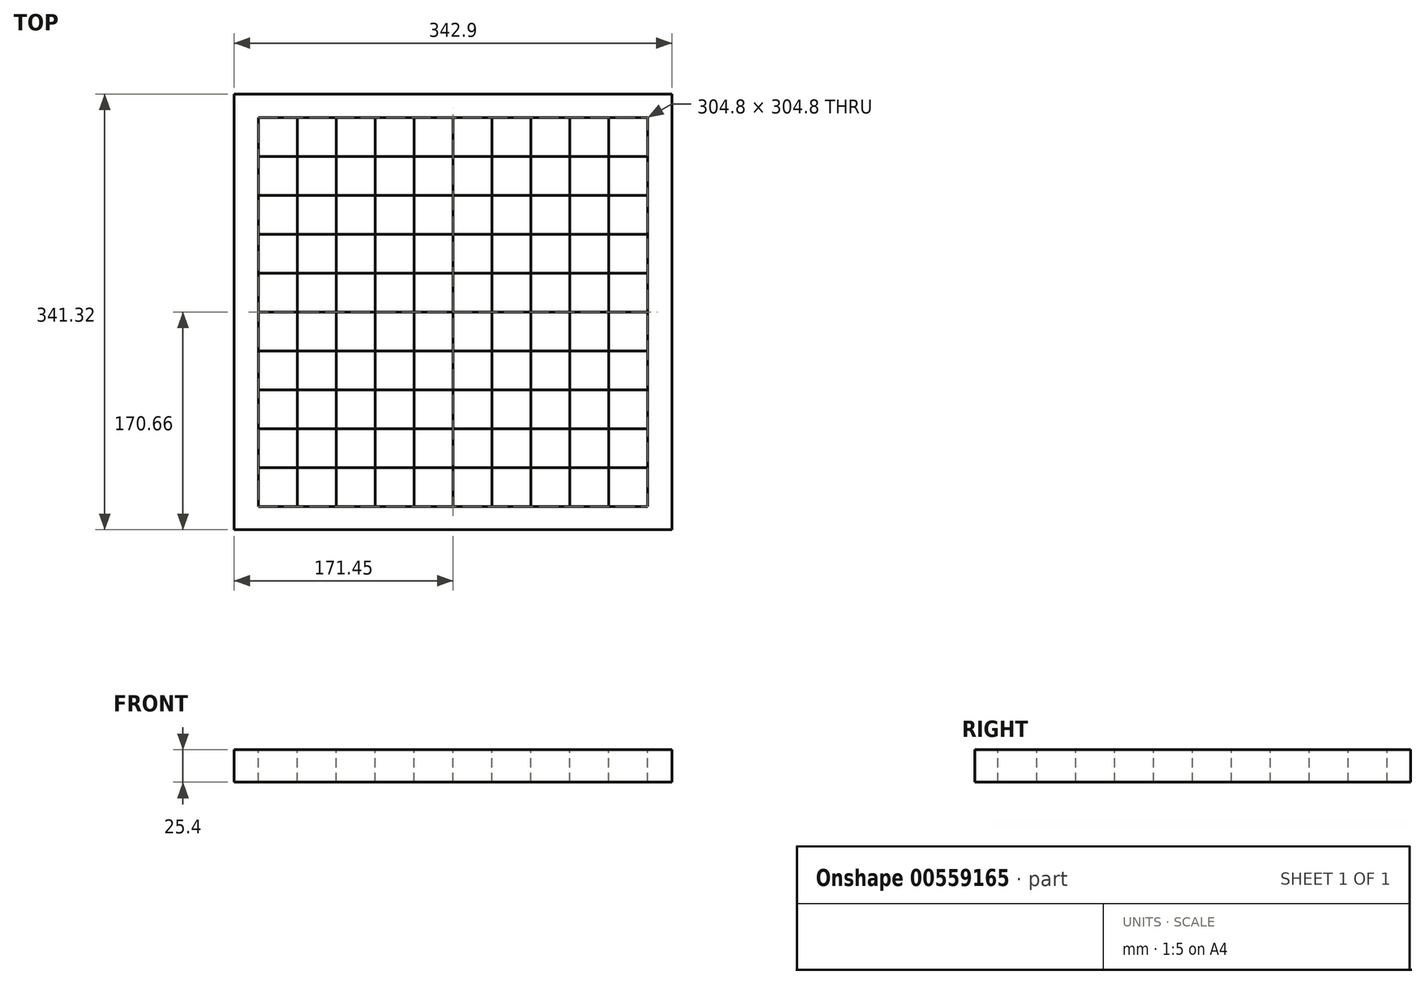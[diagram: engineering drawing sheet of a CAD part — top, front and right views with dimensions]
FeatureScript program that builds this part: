
annotation { "Feature Type Name" : "Feature", "Feature Type Description" : "" }
export const myFeature = defineFeature(function(context is Context, id is Id, definition is map)
    precondition{}
    {
        {
            var Q0;
            Q0=qCreatedBy(makeId("Top.planeOp"),FACE);
            var sketch = newSketch(context, id + "F0", { "sketchPlane" : qUnion([Q0])});
            skLineSegment(sketch, "E0.bottom", {"start": v(171.45, -170.66) * mm, "end": v(-171.45, -170.66) * mm});
            skLineSegment(sketch, "E0.top", {"start": v(171.45, 170.66) * mm, "end": v(-171.45, 170.66) * mm});
            skLineSegment(sketch, "E0.left", {"start": v(171.45, -170.66) * mm, "end": v(171.45, 170.66) * mm});
            skLineSegment(sketch, "E0.right", {"start": v(-171.45, -170.66) * mm, "end": v(-171.45, 170.66) * mm});
            skPoint(sketch, "E0.middle", {"position": v(0, 0) * mm});
            skLineSegment(sketch, "E1.bottom", {"start": v(152.4, -152.4) * mm, "end": v(-152.4, -152.4) * mm});
            skLineSegment(sketch, "E1.top", {"start": v(152.4, 152.4) * mm, "end": v(-152.4, 152.4) * mm});
            skLineSegment(sketch, "E1.left", {"start": v(152.4, -152.4) * mm, "end": v(152.4, 152.4) * mm});
            skLineSegment(sketch, "E1.right", {"start": v(-152.4, -152.4) * mm, "end": v(-152.4, 152.4) * mm});
            skSolve(sketch);
        }
        {
            var Q0;
            Q0=makeQuery(id+"F0.imprint","IMPRINT",FACE,{"disambiguationData":[TD([[makeQuery(id+"F0.imprint","IMPRINT",EDGE,{"derivedFrom":sQuery(id+"F0.wireOp",EDGE,"E1.bottom")}),-1.0]])]});
            var sketch = newSketch(context, id + "F1", { "sketchPlane" : qUnion([Q0])});
            skLineSegment(sketch, "E2.0", {"start": v(152.4, 152.4) * mm, "end": v(-152.4, 152.4) * mm});
            skLineSegment(sketch, "E3.0", {"start": v(-152.4, -152.4) * mm, "end": v(-152.4, 152.4) * mm});
            skLineSegment(sketch, "E4.0", {"start": v(152.4, -152.4) * mm, "end": v(-152.4, -152.4) * mm});
            skLineSegment(sketch, "E5.0", {"start": v(152.4, -152.4) * mm, "end": v(152.4, 152.4) * mm});
            skLineSegment(sketch, "E6", {"start": v(-121.92, 152.4) * mm, "end": v(-121.92, -152.4) * mm});
            skLineSegment(sketch, "E7", {"start": v(-91.44, 152.4) * mm, "end": v(-91.44, -152.4) * mm});
            skLineSegment(sketch, "E8", {"start": v(-60.96, 152.4) * mm, "end": v(-60.96, -152.4) * mm});
            skLineSegment(sketch, "E9", {"start": v(60.96, 152.4) * mm, "end": v(60.96, -152.4) * mm});
            skLineSegment(sketch, "E10", {"start": v(-30.48, 152.4) * mm, "end": v(-30.48, -152.4) * mm});
            skLineSegment(sketch, "E11", {"start": v(30.48, 152.4) * mm, "end": v(30.48, -152.4) * mm});
            skLineSegment(sketch, "E12", {"start": v(91.44, 152.4) * mm, "end": v(91.44, -152.4) * mm});
            skLineSegment(sketch, "E13", {"start": v(121.92, 152.4) * mm, "end": v(121.92, -152.4) * mm});
            skLineSegment(sketch, "E14", {"start": v(0, 152.4) * mm, "end": v(0, -152.4) * mm});
            skLineSegment(sketch, "E15", {"start": v(-152.4, 121.92) * mm, "end": v(152.4, 121.92) * mm});
            skLineSegment(sketch, "E16", {"start": v(-152.4, 91.44) * mm, "end": v(152.4, 91.44) * mm});
            skLineSegment(sketch, "E17.MirrorCS", {"start": v(-152.4, -121.92) * mm, "end": v(152.4, -121.92) * mm});
            skLineSegment(sketch, "E18.MirrorCS", {"start": v(-152.4, -91.44) * mm, "end": v(152.4, -91.44) * mm});
            skLineSegment(sketch, "E19", {"start": v(-152.4, 60.96) * mm, "end": v(152.4, 60.96) * mm});
            skLineSegment(sketch, "E20", {"start": v(-152.4, 30.48) * mm, "end": v(152.4, 30.48) * mm});
            skLineSegment(sketch, "E21.MirrorCS", {"start": v(-152.4, -60.96) * mm, "end": v(152.4, -60.96) * mm});
            skLineSegment(sketch, "E22.MirrorCS", {"start": v(-152.4, -30.48) * mm, "end": v(152.4, -30.48) * mm});
            skLineSegment(sketch, "E23", {"start": v(-152.4, 0) * mm, "end": v(152.4, 0) * mm});
            skSolve(sketch);
        }
        {
            var Q0;
            Q0 = qSketchRegion(id + "F0", true);
            extrude(context, id + "F2", {"entities" : qUnion([Q0]), "oppositeDirection" : true, "depth" : 25.4 * mm, "offsetDistance" : 25.4 * mm});
        }
        {
            var Q0;
            {var subQ0=sQuery(id+"F1.wireOp",EDGE,"E3.0");var subQ1=sQuery(id+"F1.wireOp",EDGE,"E2.0");var subQ2=makeQuery(id+"F1.imprint","INTERSECT",VERTEX,{"derivedFrom":[subQ1,subQ0]});Q0=makeQuery(id+"F1.imprint","IMPRINT",FACE,{"disambiguationData":[TD([[makeQuery(id+"F1.imprint","IMPRINT",EDGE,{"disambiguationData":[TD([[subQ2,1.0]])],"derivedFrom":subQ1}),1.0]])]});}
            var Q1;
            {var subQ0=sQuery(id+"F1.wireOp",EDGE,"E15");var subQ1=sQuery(id+"F1.wireOp",EDGE,"E6");var subQ2=makeQuery(id+"F1.imprint","INTERSECT",VERTEX,{"derivedFrom":[subQ1,subQ0]});Q1=makeQuery(id+"F1.imprint","IMPRINT",FACE,{"disambiguationData":[TD([[makeQuery(id+"F1.imprint","IMPRINT",EDGE,{"disambiguationData":[TD([[subQ2,-1.0]])],"derivedFrom":subQ1}),1.0]])]});}
            var Q2;
            {var subQ0=sQuery(id+"F1.wireOp",EDGE,"E7");var subQ1=sQuery(id+"F1.wireOp",EDGE,"E2.0");var subQ2=makeQuery(id+"F1.imprint","INTERSECT",VERTEX,{"derivedFrom":[subQ1,subQ0]});Q2=makeQuery(id+"F1.imprint","IMPRINT",FACE,{"disambiguationData":[TD([[makeQuery(id+"F1.imprint","IMPRINT",EDGE,{"disambiguationData":[TD([[subQ2,1.0]])],"derivedFrom":subQ1}),1.0]])]});}
            var Q3;
            {var subQ0=sQuery(id+"F1.wireOp",EDGE,"E15");var subQ1=sQuery(id+"F1.wireOp",EDGE,"E8");var subQ2=makeQuery(id+"F1.imprint","INTERSECT",VERTEX,{"derivedFrom":[subQ1,subQ0]});Q3=makeQuery(id+"F1.imprint","IMPRINT",FACE,{"disambiguationData":[TD([[makeQuery(id+"F1.imprint","IMPRINT",EDGE,{"disambiguationData":[TD([[subQ2,-1.0]])],"derivedFrom":subQ1}),1.0]])]});}
            var Q4;
            {var subQ0=sQuery(id+"F1.wireOp",EDGE,"E10");var subQ1=sQuery(id+"F1.wireOp",EDGE,"E2.0");var subQ2=makeQuery(id+"F1.imprint","INTERSECT",VERTEX,{"derivedFrom":[subQ1,subQ0]});Q4=makeQuery(id+"F1.imprint","IMPRINT",FACE,{"disambiguationData":[TD([[makeQuery(id+"F1.imprint","IMPRINT",EDGE,{"disambiguationData":[TD([[subQ2,1.0]])],"derivedFrom":subQ1}),1.0]])]});}
            var Q5;
            {var subQ0=sQuery(id+"F1.wireOp",EDGE,"E15");var subQ1=sQuery(id+"F1.wireOp",EDGE,"E11");var subQ2=makeQuery(id+"F1.imprint","INTERSECT",VERTEX,{"derivedFrom":[subQ1,subQ0]});Q5=makeQuery(id+"F1.imprint","IMPRINT",FACE,{"disambiguationData":[TD([[makeQuery(id+"F1.imprint","IMPRINT",EDGE,{"disambiguationData":[TD([[subQ2,-1.0]])],"derivedFrom":subQ1}),-1.0]])]});}
            var Q6;
            {var subQ0=sQuery(id+"F1.wireOp",EDGE,"E9");var subQ1=sQuery(id+"F1.wireOp",EDGE,"E2.0");var subQ2=makeQuery(id+"F1.imprint","INTERSECT",VERTEX,{"derivedFrom":[subQ1,subQ0]});Q6=makeQuery(id+"F1.imprint","IMPRINT",FACE,{"disambiguationData":[TD([[makeQuery(id+"F1.imprint","IMPRINT",EDGE,{"disambiguationData":[TD([[subQ2,-1.0]])],"derivedFrom":subQ1}),1.0]])]});}
            var Q7;
            {var subQ0=sQuery(id+"F1.wireOp",EDGE,"E15");var subQ1=sQuery(id+"F1.wireOp",EDGE,"E9");var subQ2=makeQuery(id+"F1.imprint","INTERSECT",VERTEX,{"derivedFrom":[subQ1,subQ0]});Q7=makeQuery(id+"F1.imprint","IMPRINT",FACE,{"disambiguationData":[TD([[makeQuery(id+"F1.imprint","IMPRINT",EDGE,{"disambiguationData":[TD([[subQ2,-1.0]])],"derivedFrom":subQ1}),1.0]])]});}
            var Q8;
            {var subQ0=sQuery(id+"F1.wireOp",EDGE,"E12");var subQ1=sQuery(id+"F1.wireOp",EDGE,"E2.0");var subQ2=makeQuery(id+"F1.imprint","INTERSECT",VERTEX,{"derivedFrom":[subQ1,subQ0]});Q8=makeQuery(id+"F1.imprint","IMPRINT",FACE,{"disambiguationData":[TD([[makeQuery(id+"F1.imprint","IMPRINT",EDGE,{"disambiguationData":[TD([[subQ2,1.0]])],"derivedFrom":subQ1}),1.0]])]});}
            var Q9;
            {var subQ0=sQuery(id+"F1.wireOp",EDGE,"E15");var subQ1=sQuery(id+"F1.wireOp",EDGE,"E5.0");var subQ2=makeQuery(id+"F1.imprint","INTERSECT",VERTEX,{"derivedFrom":[subQ1,subQ0]});Q9=makeQuery(id+"F1.imprint","IMPRINT",FACE,{"disambiguationData":[TD([[makeQuery(id+"F1.imprint","IMPRINT",EDGE,{"disambiguationData":[TD([[subQ2,1.0]])],"derivedFrom":subQ1}),1.0]])]});}
            var Q10;
            {var subQ0=sQuery(id+"F1.wireOp",EDGE,"E16");var subQ1=sQuery(id+"F1.wireOp",EDGE,"E3.0");var subQ2=makeQuery(id+"F1.imprint","INTERSECT",VERTEX,{"derivedFrom":[subQ1,subQ0]});Q10=makeQuery(id+"F1.imprint","IMPRINT",FACE,{"disambiguationData":[TD([[makeQuery(id+"F1.imprint","IMPRINT",EDGE,{"disambiguationData":[TD([[subQ2,1.0]])],"derivedFrom":subQ1}),-1.0]])]});}
            var Q11;
            {var subQ0=sQuery(id+"F1.wireOp",EDGE,"E16");var subQ1=sQuery(id+"F1.wireOp",EDGE,"E7");var subQ2=makeQuery(id+"F1.imprint","INTERSECT",VERTEX,{"derivedFrom":[subQ1,subQ0]});Q11=makeQuery(id+"F1.imprint","IMPRINT",FACE,{"disambiguationData":[TD([[makeQuery(id+"F1.imprint","IMPRINT",EDGE,{"disambiguationData":[TD([[subQ2,-1.0]])],"derivedFrom":subQ1}),1.0]])]});}
            var Q12;
            {var subQ0=sQuery(id+"F1.wireOp",EDGE,"E16");var subQ1=sQuery(id+"F1.wireOp",EDGE,"E10");var subQ2=makeQuery(id+"F1.imprint","INTERSECT",VERTEX,{"derivedFrom":[subQ1,subQ0]});Q12=makeQuery(id+"F1.imprint","IMPRINT",FACE,{"disambiguationData":[TD([[makeQuery(id+"F1.imprint","IMPRINT",EDGE,{"disambiguationData":[TD([[subQ2,-1.0]])],"derivedFrom":subQ1}),1.0]])]});}
            var Q13;
            {var subQ0=sQuery(id+"F1.wireOp",EDGE,"E16");var subQ1=sQuery(id+"F1.wireOp",EDGE,"E9");var subQ2=makeQuery(id+"F1.imprint","INTERSECT",VERTEX,{"derivedFrom":[subQ1,subQ0]});Q13=makeQuery(id+"F1.imprint","IMPRINT",FACE,{"disambiguationData":[TD([[makeQuery(id+"F1.imprint","IMPRINT",EDGE,{"disambiguationData":[TD([[subQ2,-1.0]])],"derivedFrom":subQ1}),-1.0]])]});}
            var Q14;
            {var subQ0=sQuery(id+"F1.wireOp",EDGE,"E16");var subQ1=sQuery(id+"F1.wireOp",EDGE,"E12");var subQ2=makeQuery(id+"F1.imprint","INTERSECT",VERTEX,{"derivedFrom":[subQ1,subQ0]});Q14=makeQuery(id+"F1.imprint","IMPRINT",FACE,{"disambiguationData":[TD([[makeQuery(id+"F1.imprint","IMPRINT",EDGE,{"disambiguationData":[TD([[subQ2,-1.0]])],"derivedFrom":subQ1}),1.0]])]});}
            var Q15;
            {var subQ0=sQuery(id+"F1.wireOp",EDGE,"E19");var subQ1=sQuery(id+"F1.wireOp",EDGE,"E5.0");var subQ2=makeQuery(id+"F1.imprint","INTERSECT",VERTEX,{"derivedFrom":[subQ1,subQ0]});Q15=makeQuery(id+"F1.imprint","IMPRINT",FACE,{"disambiguationData":[TD([[makeQuery(id+"F1.imprint","IMPRINT",EDGE,{"disambiguationData":[TD([[subQ2,1.0]])],"derivedFrom":subQ1}),1.0]])]});}
            var Q16;
            {var subQ0=sQuery(id+"F1.wireOp",EDGE,"E19");var subQ1=sQuery(id+"F1.wireOp",EDGE,"E9");var subQ2=makeQuery(id+"F1.imprint","INTERSECT",VERTEX,{"derivedFrom":[subQ1,subQ0]});Q16=makeQuery(id+"F1.imprint","IMPRINT",FACE,{"disambiguationData":[TD([[makeQuery(id+"F1.imprint","IMPRINT",EDGE,{"disambiguationData":[TD([[subQ2,-1.0]])],"derivedFrom":subQ1}),1.0]])]});}
            var Q17;
            {var subQ0=sQuery(id+"F1.wireOp",EDGE,"E19");var subQ1=sQuery(id+"F1.wireOp",EDGE,"E11");var subQ2=makeQuery(id+"F1.imprint","INTERSECT",VERTEX,{"derivedFrom":[subQ1,subQ0]});Q17=makeQuery(id+"F1.imprint","IMPRINT",FACE,{"disambiguationData":[TD([[makeQuery(id+"F1.imprint","IMPRINT",EDGE,{"disambiguationData":[TD([[subQ2,-1.0]])],"derivedFrom":subQ1}),-1.0]])]});}
            var Q18;
            {var subQ0=sQuery(id+"F1.wireOp",EDGE,"E19");var subQ1=sQuery(id+"F1.wireOp",EDGE,"E8");var subQ2=makeQuery(id+"F1.imprint","INTERSECT",VERTEX,{"derivedFrom":[subQ1,subQ0]});Q18=makeQuery(id+"F1.imprint","IMPRINT",FACE,{"disambiguationData":[TD([[makeQuery(id+"F1.imprint","IMPRINT",EDGE,{"disambiguationData":[TD([[subQ2,-1.0]])],"derivedFrom":subQ1}),1.0]])]});}
            var Q19;
            {var subQ0=sQuery(id+"F1.wireOp",EDGE,"E19");var subQ1=sQuery(id+"F1.wireOp",EDGE,"E6");var subQ2=makeQuery(id+"F1.imprint","INTERSECT",VERTEX,{"derivedFrom":[subQ1,subQ0]});Q19=makeQuery(id+"F1.imprint","IMPRINT",FACE,{"disambiguationData":[TD([[makeQuery(id+"F1.imprint","IMPRINT",EDGE,{"disambiguationData":[TD([[subQ2,-1.0]])],"derivedFrom":subQ1}),1.0]])]});}
            var Q20;
            {var subQ0=sQuery(id+"F1.wireOp",EDGE,"E20");var subQ1=sQuery(id+"F1.wireOp",EDGE,"E3.0");var subQ2=makeQuery(id+"F1.imprint","INTERSECT",VERTEX,{"derivedFrom":[subQ1,subQ0]});Q20=makeQuery(id+"F1.imprint","IMPRINT",FACE,{"disambiguationData":[TD([[makeQuery(id+"F1.imprint","IMPRINT",EDGE,{"disambiguationData":[TD([[subQ2,1.0]])],"derivedFrom":subQ1}),-1.0]])]});}
            var Q21;
            {var subQ0=sQuery(id+"F1.wireOp",EDGE,"E20");var subQ1=sQuery(id+"F1.wireOp",EDGE,"E7");var subQ2=makeQuery(id+"F1.imprint","INTERSECT",VERTEX,{"derivedFrom":[subQ1,subQ0]});Q21=makeQuery(id+"F1.imprint","IMPRINT",FACE,{"disambiguationData":[TD([[makeQuery(id+"F1.imprint","IMPRINT",EDGE,{"disambiguationData":[TD([[subQ2,-1.0]])],"derivedFrom":subQ1}),1.0]])]});}
            var Q22;
            {var subQ0=sQuery(id+"F1.wireOp",EDGE,"E20");var subQ1=sQuery(id+"F1.wireOp",EDGE,"E10");var subQ2=makeQuery(id+"F1.imprint","INTERSECT",VERTEX,{"derivedFrom":[subQ1,subQ0]});Q22=makeQuery(id+"F1.imprint","IMPRINT",FACE,{"disambiguationData":[TD([[makeQuery(id+"F1.imprint","IMPRINT",EDGE,{"disambiguationData":[TD([[subQ2,-1.0]])],"derivedFrom":subQ1}),1.0]])]});}
            var Q23;
            {var subQ0=sQuery(id+"F1.wireOp",EDGE,"E20");var subQ1=sQuery(id+"F1.wireOp",EDGE,"E9");var subQ2=makeQuery(id+"F1.imprint","INTERSECT",VERTEX,{"derivedFrom":[subQ1,subQ0]});Q23=makeQuery(id+"F1.imprint","IMPRINT",FACE,{"disambiguationData":[TD([[makeQuery(id+"F1.imprint","IMPRINT",EDGE,{"disambiguationData":[TD([[subQ2,-1.0]])],"derivedFrom":subQ1}),-1.0]])]});}
            var Q24;
            {var subQ0=sQuery(id+"F1.wireOp",EDGE,"E20");var subQ1=sQuery(id+"F1.wireOp",EDGE,"E12");var subQ2=makeQuery(id+"F1.imprint","INTERSECT",VERTEX,{"derivedFrom":[subQ1,subQ0]});Q24=makeQuery(id+"F1.imprint","IMPRINT",FACE,{"disambiguationData":[TD([[makeQuery(id+"F1.imprint","IMPRINT",EDGE,{"disambiguationData":[TD([[subQ2,-1.0]])],"derivedFrom":subQ1}),1.0]])]});}
            var Q25;
            {var subQ0=sQuery(id+"F1.wireOp",EDGE,"E22.MirrorCS");var subQ1=sQuery(id+"F1.wireOp",EDGE,"E5.0");var subQ2=makeQuery(id+"F1.imprint","INTERSECT",VERTEX,{"derivedFrom":[subQ1,subQ0]});Q25=makeQuery(id+"F1.imprint","IMPRINT",FACE,{"disambiguationData":[TD([[makeQuery(id+"F1.imprint","IMPRINT",EDGE,{"disambiguationData":[TD([[subQ2,-1.0]])],"derivedFrom":subQ1}),1.0]])]});}
            var Q26;
            {var subQ0=sQuery(id+"F1.wireOp",EDGE,"E23");var subQ1=sQuery(id+"F1.wireOp",EDGE,"E9");var subQ2=makeQuery(id+"F1.imprint","INTERSECT",VERTEX,{"derivedFrom":[subQ1,subQ0]});Q26=makeQuery(id+"F1.imprint","IMPRINT",FACE,{"disambiguationData":[TD([[makeQuery(id+"F1.imprint","IMPRINT",EDGE,{"disambiguationData":[TD([[subQ2,-1.0]])],"derivedFrom":subQ1}),1.0]])]});}
            var Q27;
            {var subQ0=sQuery(id+"F1.wireOp",EDGE,"E23");var subQ1=sQuery(id+"F1.wireOp",EDGE,"E11");var subQ2=makeQuery(id+"F1.imprint","INTERSECT",VERTEX,{"derivedFrom":[subQ1,subQ0]});Q27=makeQuery(id+"F1.imprint","IMPRINT",FACE,{"disambiguationData":[TD([[makeQuery(id+"F1.imprint","IMPRINT",EDGE,{"disambiguationData":[TD([[subQ2,-1.0]])],"derivedFrom":subQ1}),-1.0]])]});}
            var Q28;
            {var subQ0=sQuery(id+"F1.wireOp",EDGE,"E23");var subQ1=sQuery(id+"F1.wireOp",EDGE,"E8");var subQ2=makeQuery(id+"F1.imprint","INTERSECT",VERTEX,{"derivedFrom":[subQ1,subQ0]});Q28=makeQuery(id+"F1.imprint","IMPRINT",FACE,{"disambiguationData":[TD([[makeQuery(id+"F1.imprint","IMPRINT",EDGE,{"disambiguationData":[TD([[subQ2,-1.0]])],"derivedFrom":subQ1}),1.0]])]});}
            var Q29;
            {var subQ0=sQuery(id+"F1.wireOp",EDGE,"E23");var subQ1=sQuery(id+"F1.wireOp",EDGE,"E6");var subQ2=makeQuery(id+"F1.imprint","INTERSECT",VERTEX,{"derivedFrom":[subQ1,subQ0]});Q29=makeQuery(id+"F1.imprint","IMPRINT",FACE,{"disambiguationData":[TD([[makeQuery(id+"F1.imprint","IMPRINT",EDGE,{"disambiguationData":[TD([[subQ2,-1.0]])],"derivedFrom":subQ1}),1.0]])]});}
            var Q30;
            {var subQ0=sQuery(id+"F1.wireOp",EDGE,"E21.MirrorCS");var subQ1=sQuery(id+"F1.wireOp",EDGE,"E3.0");var subQ2=makeQuery(id+"F1.imprint","INTERSECT",VERTEX,{"derivedFrom":[subQ1,subQ0]});Q30=makeQuery(id+"F1.imprint","IMPRINT",FACE,{"disambiguationData":[TD([[makeQuery(id+"F1.imprint","IMPRINT",EDGE,{"disambiguationData":[TD([[subQ2,-1.0]])],"derivedFrom":subQ1}),-1.0]])]});}
            var Q31;
            {var subQ0=sQuery(id+"F1.wireOp",EDGE,"E22.MirrorCS");var subQ1=sQuery(id+"F1.wireOp",EDGE,"E7");var subQ2=makeQuery(id+"F1.imprint","INTERSECT",VERTEX,{"derivedFrom":[subQ1,subQ0]});Q31=makeQuery(id+"F1.imprint","IMPRINT",FACE,{"disambiguationData":[TD([[makeQuery(id+"F1.imprint","IMPRINT",EDGE,{"disambiguationData":[TD([[subQ2,-1.0]])],"derivedFrom":subQ1}),1.0]])]});}
            var Q32;
            {var subQ0=sQuery(id+"F1.wireOp",EDGE,"E22.MirrorCS");var subQ1=sQuery(id+"F1.wireOp",EDGE,"E10");var subQ2=makeQuery(id+"F1.imprint","INTERSECT",VERTEX,{"derivedFrom":[subQ1,subQ0]});Q32=makeQuery(id+"F1.imprint","IMPRINT",FACE,{"disambiguationData":[TD([[makeQuery(id+"F1.imprint","IMPRINT",EDGE,{"disambiguationData":[TD([[subQ2,-1.0]])],"derivedFrom":subQ1}),1.0]])]});}
            var Q33;
            {var subQ0=sQuery(id+"F1.wireOp",EDGE,"E22.MirrorCS");var subQ1=sQuery(id+"F1.wireOp",EDGE,"E9");var subQ2=makeQuery(id+"F1.imprint","INTERSECT",VERTEX,{"derivedFrom":[subQ1,subQ0]});Q33=makeQuery(id+"F1.imprint","IMPRINT",FACE,{"disambiguationData":[TD([[makeQuery(id+"F1.imprint","IMPRINT",EDGE,{"disambiguationData":[TD([[subQ2,-1.0]])],"derivedFrom":subQ1}),-1.0]])]});}
            var Q34;
            {var subQ0=sQuery(id+"F1.wireOp",EDGE,"E22.MirrorCS");var subQ1=sQuery(id+"F1.wireOp",EDGE,"E12");var subQ2=makeQuery(id+"F1.imprint","INTERSECT",VERTEX,{"derivedFrom":[subQ1,subQ0]});Q34=makeQuery(id+"F1.imprint","IMPRINT",FACE,{"disambiguationData":[TD([[makeQuery(id+"F1.imprint","IMPRINT",EDGE,{"disambiguationData":[TD([[subQ2,-1.0]])],"derivedFrom":subQ1}),1.0]])]});}
            var Q35;
            {var subQ0=sQuery(id+"F1.wireOp",EDGE,"E18.MirrorCS");var subQ1=sQuery(id+"F1.wireOp",EDGE,"E5.0");var subQ2=makeQuery(id+"F1.imprint","INTERSECT",VERTEX,{"derivedFrom":[subQ1,subQ0]});Q35=makeQuery(id+"F1.imprint","IMPRINT",FACE,{"disambiguationData":[TD([[makeQuery(id+"F1.imprint","IMPRINT",EDGE,{"disambiguationData":[TD([[subQ2,-1.0]])],"derivedFrom":subQ1}),1.0]])]});}
            var Q36;
            {var subQ0=sQuery(id+"F1.wireOp",EDGE,"E21.MirrorCS");var subQ1=sQuery(id+"F1.wireOp",EDGE,"E9");var subQ2=makeQuery(id+"F1.imprint","INTERSECT",VERTEX,{"derivedFrom":[subQ1,subQ0]});Q36=makeQuery(id+"F1.imprint","IMPRINT",FACE,{"disambiguationData":[TD([[makeQuery(id+"F1.imprint","IMPRINT",EDGE,{"disambiguationData":[TD([[subQ2,-1.0]])],"derivedFrom":subQ1}),1.0]])]});}
            var Q37;
            {var subQ0=sQuery(id+"F1.wireOp",EDGE,"E21.MirrorCS");var subQ1=sQuery(id+"F1.wireOp",EDGE,"E11");var subQ2=makeQuery(id+"F1.imprint","INTERSECT",VERTEX,{"derivedFrom":[subQ1,subQ0]});Q37=makeQuery(id+"F1.imprint","IMPRINT",FACE,{"disambiguationData":[TD([[makeQuery(id+"F1.imprint","IMPRINT",EDGE,{"disambiguationData":[TD([[subQ2,-1.0]])],"derivedFrom":subQ1}),-1.0]])]});}
            var Q38;
            {var subQ0=sQuery(id+"F1.wireOp",EDGE,"E21.MirrorCS");var subQ1=sQuery(id+"F1.wireOp",EDGE,"E8");var subQ2=makeQuery(id+"F1.imprint","INTERSECT",VERTEX,{"derivedFrom":[subQ1,subQ0]});Q38=makeQuery(id+"F1.imprint","IMPRINT",FACE,{"disambiguationData":[TD([[makeQuery(id+"F1.imprint","IMPRINT",EDGE,{"disambiguationData":[TD([[subQ2,-1.0]])],"derivedFrom":subQ1}),1.0]])]});}
            var Q39;
            {var subQ0=sQuery(id+"F1.wireOp",EDGE,"E21.MirrorCS");var subQ1=sQuery(id+"F1.wireOp",EDGE,"E6");var subQ2=makeQuery(id+"F1.imprint","INTERSECT",VERTEX,{"derivedFrom":[subQ1,subQ0]});Q39=makeQuery(id+"F1.imprint","IMPRINT",FACE,{"disambiguationData":[TD([[makeQuery(id+"F1.imprint","IMPRINT",EDGE,{"disambiguationData":[TD([[subQ2,-1.0]])],"derivedFrom":subQ1}),1.0]])]});}
            var Q40;
            {var subQ0=sQuery(id+"F1.wireOp",EDGE,"E17.MirrorCS");var subQ1=sQuery(id+"F1.wireOp",EDGE,"E3.0");var subQ2=makeQuery(id+"F1.imprint","INTERSECT",VERTEX,{"derivedFrom":[subQ1,subQ0]});Q40=makeQuery(id+"F1.imprint","IMPRINT",FACE,{"disambiguationData":[TD([[makeQuery(id+"F1.imprint","IMPRINT",EDGE,{"disambiguationData":[TD([[subQ2,-1.0]])],"derivedFrom":subQ1}),-1.0]])]});}
            var Q41;
            {var subQ0=sQuery(id+"F1.wireOp",EDGE,"E18.MirrorCS");var subQ1=sQuery(id+"F1.wireOp",EDGE,"E7");var subQ2=makeQuery(id+"F1.imprint","INTERSECT",VERTEX,{"derivedFrom":[subQ1,subQ0]});Q41=makeQuery(id+"F1.imprint","IMPRINT",FACE,{"disambiguationData":[TD([[makeQuery(id+"F1.imprint","IMPRINT",EDGE,{"disambiguationData":[TD([[subQ2,-1.0]])],"derivedFrom":subQ1}),1.0]])]});}
            var Q42;
            {var subQ0=sQuery(id+"F1.wireOp",EDGE,"E18.MirrorCS");var subQ1=sQuery(id+"F1.wireOp",EDGE,"E10");var subQ2=makeQuery(id+"F1.imprint","INTERSECT",VERTEX,{"derivedFrom":[subQ1,subQ0]});Q42=makeQuery(id+"F1.imprint","IMPRINT",FACE,{"disambiguationData":[TD([[makeQuery(id+"F1.imprint","IMPRINT",EDGE,{"disambiguationData":[TD([[subQ2,-1.0]])],"derivedFrom":subQ1}),1.0]])]});}
            var Q43;
            {var subQ0=sQuery(id+"F1.wireOp",EDGE,"E18.MirrorCS");var subQ1=sQuery(id+"F1.wireOp",EDGE,"E9");var subQ2=makeQuery(id+"F1.imprint","INTERSECT",VERTEX,{"derivedFrom":[subQ1,subQ0]});Q43=makeQuery(id+"F1.imprint","IMPRINT",FACE,{"disambiguationData":[TD([[makeQuery(id+"F1.imprint","IMPRINT",EDGE,{"disambiguationData":[TD([[subQ2,-1.0]])],"derivedFrom":subQ1}),-1.0]])]});}
            var Q44;
            {var subQ0=sQuery(id+"F1.wireOp",EDGE,"E18.MirrorCS");var subQ1=sQuery(id+"F1.wireOp",EDGE,"E12");var subQ2=makeQuery(id+"F1.imprint","INTERSECT",VERTEX,{"derivedFrom":[subQ1,subQ0]});Q44=makeQuery(id+"F1.imprint","IMPRINT",FACE,{"disambiguationData":[TD([[makeQuery(id+"F1.imprint","IMPRINT",EDGE,{"disambiguationData":[TD([[subQ2,-1.0]])],"derivedFrom":subQ1}),1.0]])]});}
            var Q45;
            {var subQ0=sQuery(id+"F1.wireOp",EDGE,"E5.0");var subQ1=sQuery(id+"F1.wireOp",EDGE,"E4.0");var subQ2=makeQuery(id+"F1.imprint","INTERSECT",VERTEX,{"derivedFrom":[subQ1,subQ0]});Q45=makeQuery(id+"F1.imprint","IMPRINT",FACE,{"disambiguationData":[TD([[makeQuery(id+"F1.imprint","IMPRINT",EDGE,{"disambiguationData":[TD([[subQ2,-1.0]])],"derivedFrom":subQ1}),-1.0]])]});}
            var Q46;
            {var subQ0=sQuery(id+"F1.wireOp",EDGE,"E9");var subQ1=sQuery(id+"F1.wireOp",EDGE,"E4.0");var subQ2=makeQuery(id+"F1.imprint","INTERSECT",VERTEX,{"derivedFrom":[subQ1,subQ0]});Q46=makeQuery(id+"F1.imprint","IMPRINT",FACE,{"disambiguationData":[TD([[makeQuery(id+"F1.imprint","IMPRINT",EDGE,{"disambiguationData":[TD([[subQ2,1.0]])],"derivedFrom":subQ1}),-1.0]])]});}
            var Q47;
            {var subQ0=sQuery(id+"F1.wireOp",EDGE,"E11");var subQ1=sQuery(id+"F1.wireOp",EDGE,"E4.0");var subQ2=makeQuery(id+"F1.imprint","INTERSECT",VERTEX,{"derivedFrom":[subQ1,subQ0]});Q47=makeQuery(id+"F1.imprint","IMPRINT",FACE,{"disambiguationData":[TD([[makeQuery(id+"F1.imprint","IMPRINT",EDGE,{"disambiguationData":[TD([[subQ2,-1.0]])],"derivedFrom":subQ1}),-1.0]])]});}
            var Q48;
            {var subQ0=sQuery(id+"F1.wireOp",EDGE,"E8");var subQ1=sQuery(id+"F1.wireOp",EDGE,"E4.0");var subQ2=makeQuery(id+"F1.imprint","INTERSECT",VERTEX,{"derivedFrom":[subQ1,subQ0]});Q48=makeQuery(id+"F1.imprint","IMPRINT",FACE,{"disambiguationData":[TD([[makeQuery(id+"F1.imprint","IMPRINT",EDGE,{"disambiguationData":[TD([[subQ2,1.0]])],"derivedFrom":subQ1}),-1.0]])]});}
            var Q49;
            {var subQ0=sQuery(id+"F1.wireOp",EDGE,"E6");var subQ1=sQuery(id+"F1.wireOp",EDGE,"E4.0");var subQ2=makeQuery(id+"F1.imprint","INTERSECT",VERTEX,{"derivedFrom":[subQ1,subQ0]});Q49=makeQuery(id+"F1.imprint","IMPRINT",FACE,{"disambiguationData":[TD([[makeQuery(id+"F1.imprint","IMPRINT",EDGE,{"disambiguationData":[TD([[subQ2,1.0]])],"derivedFrom":subQ1}),-1.0]])]});}
            extrude(context, id + "F3", {"entities" : qUnion([Q0, Q1, Q2, Q3, Q4, Q5, Q6, Q7, Q8, Q9, Q10, Q11, Q12, Q13, Q14, Q15, Q16, Q17, Q18, Q19, Q20, Q21, Q22, Q23, Q24, Q25, Q26, Q27, Q28, Q29, Q30, Q31, Q32, Q33, Q34, Q35, Q36, Q37, Q38, Q39, Q40, Q41, Q42, Q43, Q44, Q45, Q46, Q47, Q48, Q49]), "oppositeDirection" : true, "depth" : 25.4 * mm, "offsetDistance" : 25.4 * mm});
        }
    });
